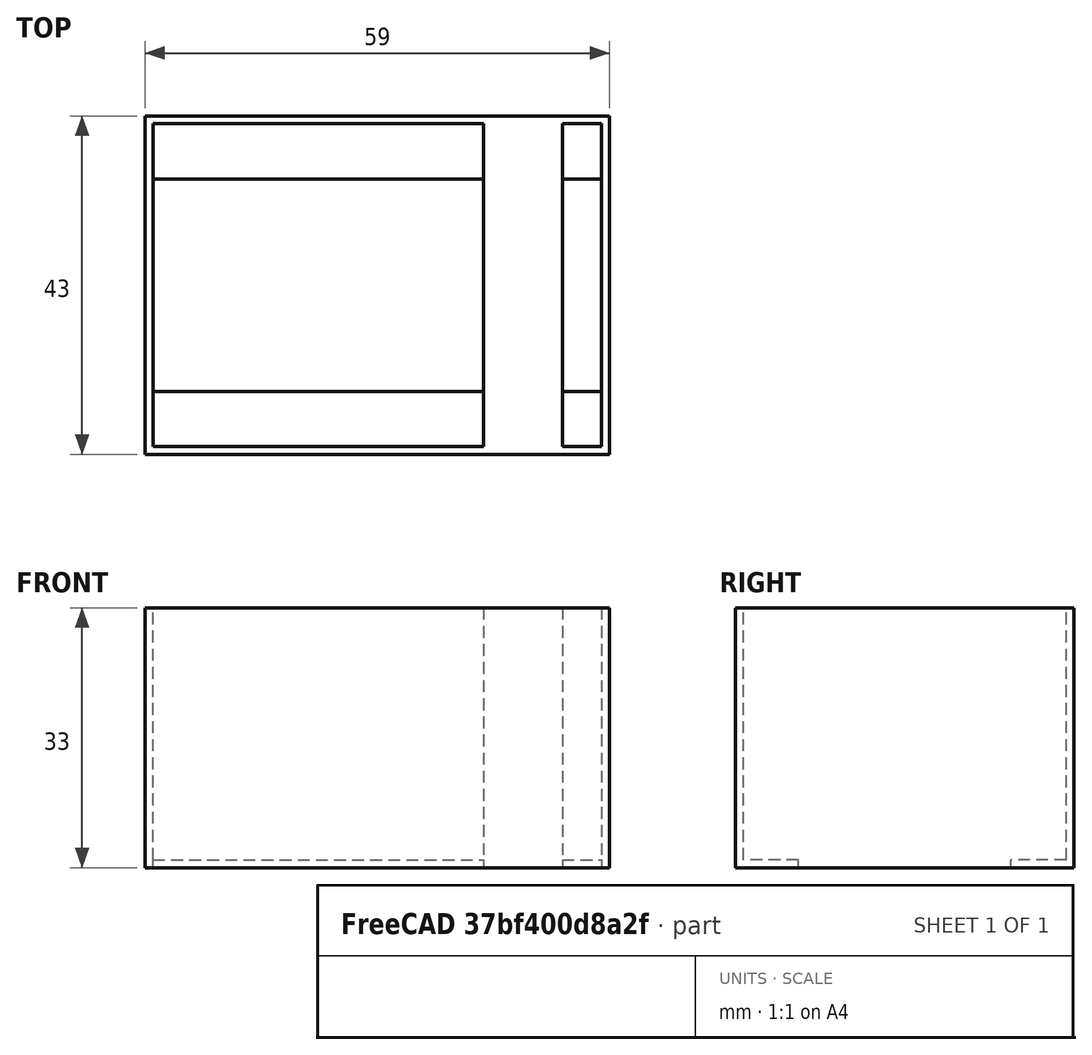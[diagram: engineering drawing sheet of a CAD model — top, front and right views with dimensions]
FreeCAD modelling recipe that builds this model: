
FCSTD DOCUMENT  (FreeCAD 0.18R4 (GitTag))
Label: dungeon
License: All rights reserved
LicenseURL: http://en.wikipedia.org/wiki/All_rights_reserved
objects: Part::Box×7, Part::Cut×2, Part::MultiFuse×2
note: 11 computed .brp shape members not serialized (recipe doc carries the construction recipe); baked Part::Feature solids carry a one-line shape summary decoded from their .brp

FEATURE [Part::Box] Box  label="Cube"
  AttacherType = Attacher::AttachEngine3D
  Height = 33
  Length = 202
  Width = 43
FEATURE [Part::Box] Box001  label="Cube001"
  AttacherType = Attacher::AttachEngine3D
  Height = 33
  Length = 200
  Placement = pos=(1,1,0) rot=(0,0,1;0rad)
  Width = 41
FEATURE [Part::Cut] Cut
  Base = -> Box
  Tool = -> Box001
FEATURE [Part::Box] Box002  label="Cube002"
  AttacherType = Attacher::AttachEngine3D
  Height = 1
  Length = 202
  Width = 8
FEATURE [Part::Box] Box003  label="Cube003"
  AttacherType = Attacher::AttachEngine3D
  Height = 1
  Length = 202
  Placement = pos=(0,35,0) rot=(0,0,1;0rad)
  Width = 8
FEATURE [Part::MultiFuse] Fusion
  Shapes = -> [Cut,Box002,Box003]
FEATURE [Part::Box] Box004  label="Cube004"
  AttacherType = Attacher::AttachEngine3D
  Height = 33
  Length = 10
  Placement = pos=(43,0,0) rot=(0,0,1;0rad)
  Width = 43
FEATURE [Part::Box] Box005  label="Cube005"
  AttacherType = Attacher::AttachEngine3D
  Height = 33
  Length = 10
  Placement = pos=(58,0,0) rot=(0,0,1;0rad)
  Width = 43
FEATURE [Part::Box] Box006  label="Cube006"
  AttacherType = Attacher::AttachEngine3D
  Height = 33
  Length = 143
  Placement = pos=(59,0,0) rot=(0,0,1;0rad)
  Width = 43
FEATURE [Part::MultiFuse] Fusion001
  Shapes = -> [Fusion,Box004,Box005]
FEATURE [Part::Cut] Cut001
  Base = -> Fusion001
  Tool = -> Box006
